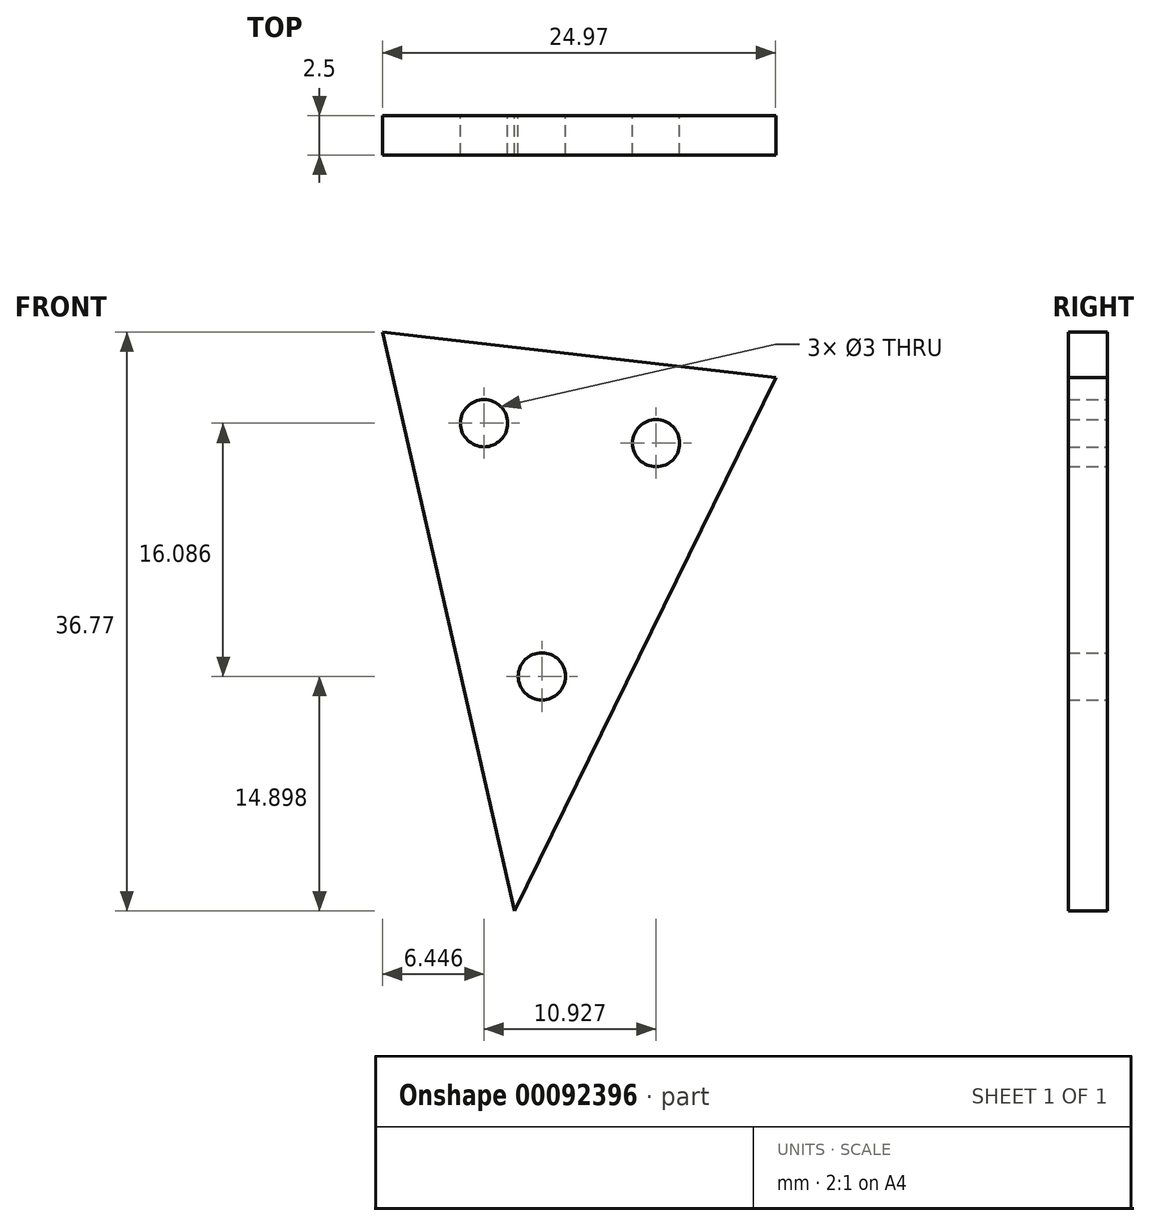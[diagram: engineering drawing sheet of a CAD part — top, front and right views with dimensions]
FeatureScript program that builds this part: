
annotation { "Feature Type Name" : "Feature", "Feature Type Description" : "" }
export const myFeature = defineFeature(function(context is Context, id is Id, definition is map)
    precondition{}
    {
        {
            var Q0;
            Q0=qCreatedBy(makeId("Front.planeOp"),FACE);
            var sketch = newSketch(context, id + "F0", { "sketchPlane" : qUnion([Q0])});
            skCircle(sketch, "E0", {"center": v(-25.46, 34.24) * mm, "radius": 1.5 * mm});
            skCircle(sketch, "E1", {"center": v(-14.54, 32.98) * mm, "radius": 1.5 * mm});
            skCircle(sketch, "E2", {"center": v(-21.8, 18.16) * mm, "radius": 1.5 * mm});
            skLineSegment(sketch, "E3.0", {"start": v(-31.91, 40.03) * mm, "end": v(-6.94, 37.13) * mm});
            skLineSegment(sketch, "E3.1", {"start": v(-23.52, 3.26) * mm, "end": v(-31.91, 40.03) * mm});
            skLineSegment(sketch, "E3.2", {"start": v(-6.94, 37.13) * mm, "end": v(-23.52, 3.26) * mm});
            skSolve(sketch);
        }
        {
            var Q0;
            Q0=makeQuery(id+"F0.imprint","IMPRINT",FACE,{"disambiguationData":[TD([[makeQuery(id+"F0.imprint","IMPRINT",EDGE,{"derivedFrom":sQuery(id+"F0.wireOp",EDGE,"E0")}),-1.0]])]});
            extrude(context, id + "F1", {"entities" : qUnion([Q0]), "endBound" : BoundingType.SYMMETRIC, "depth" : 2.5 * mm});
        }
    });
